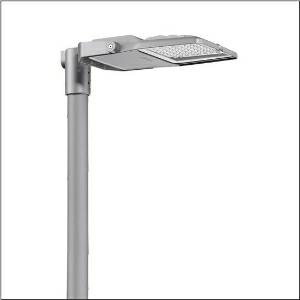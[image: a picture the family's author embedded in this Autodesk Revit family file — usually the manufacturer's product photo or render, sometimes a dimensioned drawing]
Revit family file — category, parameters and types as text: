
# Revit family: floodlight_fl_21_mini___pl43_5xa7775d2a3a_0001
name_source: partatom
category: Lighting Fixtures
units: mm (PartAtom-declared; Revit-internal decimal feet)

## family parameters
Cut with Voids When Loaded = No
Host = Face
Light Source = No
Part Type = Normal
Room Calculation Point = No
Round Connector Dimension = Use Diameter
Shared = No

## types (1)
- --- (1 x LED, 18300 lm, 142.9 W, 3000K)
    Apparent Load = 143 VA
    CIE Flux Codes = 27 78 99 100 100
    Color Rendering = 70
    Color Temperature = 3000K
    Default Elevation = 1800 mm
    Description = Floodlight FL 21 mini, floodlight, primary light control with lens, of PMMA, primary optical cover: protective disc, of toughened safety glass, transparent, light distribution: PL43, light emission: direct distribution, installation type: surface-mounted, LED, High Power LED, rated luminous flux: 18.300lm, luminous efficacy: 128lm/W, light colour: 730, colour temperature: 3000K, control gear: Smart Interface (Zhaga), control: flexible luminous flux parameterisation, time-dependent luminous flux control, constant luminous flux control, overheat protection, pre-setting: logarithmic dimming characteristic, with terminal, 6-pole, mains connection: 220..240V, AC, 50/60Hz, start of lifetime: 143W, end of service life: 151W, reduction: 63W, luminaire housing, of diecast aluminium, powder-coated, SITECO metallic grey (DB 702S), corrosivity category C5 mid according to DIN EN ISO 12944, suitable for swimming pools, chlorine-resistant, sealing non-destructively replaceable, please order mast flange separately, mast bracket, of steel, galvanised, powder-coated, SITECO metallic grey (DB 702S), Smart Interface above, protection rating (complete): IP66, insulation class (complete): insulation class II (safety insulation), certification: CE, ENEC, VDE, protection symbol: D, impact resistance: IK08, permissible operating ambient temperature: -40..+40°C, permissible operating ambient temperature for outdoor applications: -40..+50°C, standard: DIN EN 12944, LABS conformity tested according to VDMA 24364:2018-05, packaging unit: 1 piece

Light Distribution: PL43
    Height = 70 mm
    Lamp = 1 x LED
    Lamp Light Flux = 18300 lm
    Lamp Power = 142.9 W
    Lamp count = 1
    Length = 485 mm
    Luminous efficacy = 128 lm/W
    Manufacturer = Siteco
    ModVariant = No
    Model = 5XA7775D2A3A
    Number of Poles = 1
    OnlyDefault = Yes
    Power Factor = 1
    Product Name = Floodlight FL 21 mini | PL43
    Product group = floodlight | pylon annexe
    ProductGroupID = 6201
    Protection Class = Protection class II
    Protection Degree = IP 66
    RLX_Detail_Level = 1
    RLX_Emergency_Light_Flux = 0 lm
    RLX_Emergency_Type = 0
    RLX_Emergency_Type_DB = No
    RlxData = <blob elided: 101353 chars, md5=ec2046f6>
    Socket = socket
    Standby Power = 0 W
    System Light Flux = 18300 lm
    System Power = 143 W
    Type Comments = factory setting: luminous flux: 100 % | dim-lin: 254 | 730 mA
    Type Image = l_1007125.jpg
    URL = http://relux.com
    VarID = @adj_160441
    Voltage = 0 V
    Weight = 0.00 kg
    Width = 337 mm

## geometry (parser evidence)
native form markers: Blend x4, Sweep x12
no freeform markers — native parametric forms only
